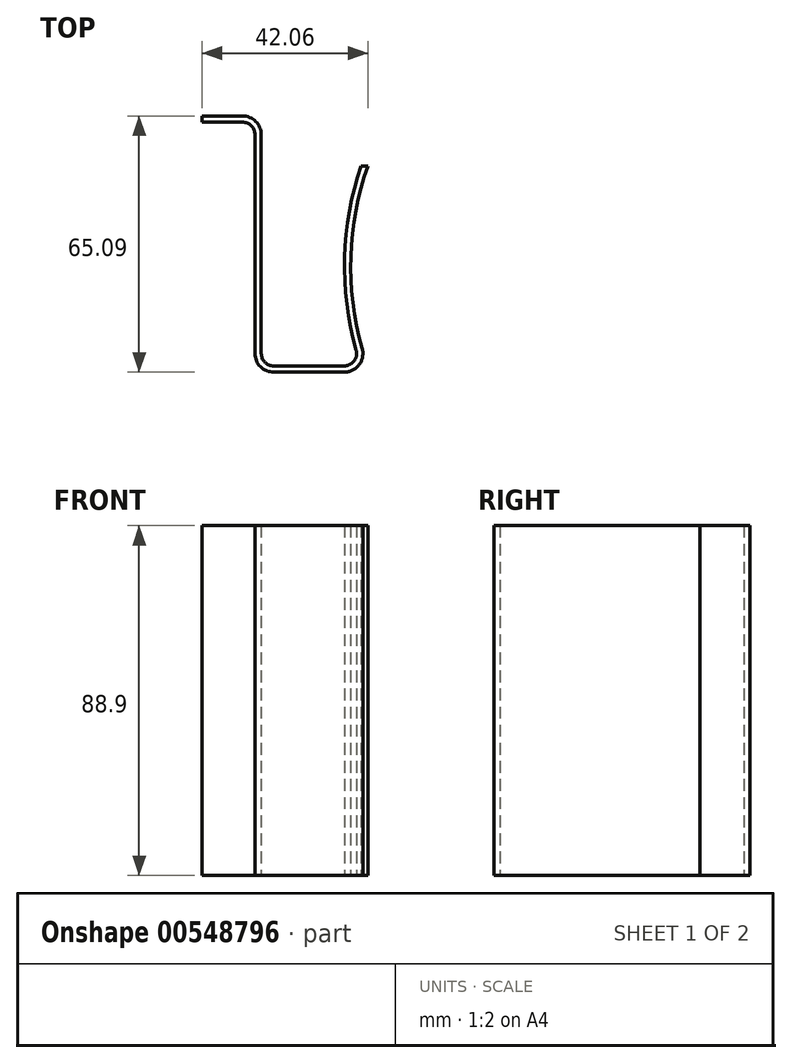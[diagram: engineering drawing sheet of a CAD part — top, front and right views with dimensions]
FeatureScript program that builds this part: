
annotation { "Feature Type Name" : "Feature", "Feature Type Description" : "" }
export const myFeature = defineFeature(function(context is Context, id is Id, definition is map)
    precondition{}
    {
        {
            var Q0;
            Q0=qCreatedBy(makeId("Top.planeOp"),FACE);
            var sketch = newSketch(context, id + "F0", { "sketchPlane" : qUnion([Q0])});
            skLineSegment(sketch, "E0", {"start": v(0, 0) * mm, "end": v(10.22, 0) * mm});
            skLineSegment(sketch, "E1", {"start": v(13.4, -3.18) * mm, "end": v(13.4, -58.74) * mm});
            skLineSegment(sketch, "E2", {"start": v(18.16, -63.5) * mm, "end": v(36.05, -63.5) * mm});
            skLineSegment(sketch, "E3", {"start": v(36.05, -61.91) * mm, "end": v(18.16, -61.91) * mm});
            skLineSegment(sketch, "E4", {"start": v(14.98, -58.74) * mm, "end": v(14.98, -3.18) * mm});
            skLineSegment(sketch, "E5", {"start": v(10.22, 1.59) * mm, "end": v(0, 1.59) * mm});
            skLineSegment(sketch, "E6", {"start": v(0, 1.59) * mm, "end": v(0, 0) * mm});
            skLineSegment(sketch, "E7", {"start": v(13.4, -31.75) * mm, "end": v(14.98, -31.75) * mm, "construction": true});
            skLineSegment(sketch, "E8", {"start": v(27.68, -61.91) * mm, "end": v(27.68, -63.5) * mm, "construction": true});
            skArc(sketch, "E9", {"start": v(40.38, -11.11) * mm, "mid": v(36.15, -34.4) * mm, "end": v(39.1, -57.87) * mm});
            skArc(sketch, "E10", {"start": v(42.06, -11.11) * mm, "mid": v(37.74, -34.16) * mm, "end": v(40.63, -57.43) * mm});
            skLineSegment(sketch, "E11", {"start": v(40.38, -61.91) * mm, "end": v(42.65, -61.91) * mm, "construction": true});
            skLineSegment(sketch, "E12", {"start": v(42.65, -61.91) * mm, "end": v(42.65, -63.5) * mm, "construction": true});
            skLineSegment(sketch, "E13", {"start": v(40.38, -11.11) * mm, "end": v(42.06, -11.11) * mm});
            skLineSegment(sketch, "E14", {"start": v(36.12, -36.51) * mm, "end": v(37.7, -36.51) * mm, "construction": true});
            skPoint(sketch, "E15.visualSharp", {"position": v(40.38, -61.91) * mm});
            skArc(sketch, "E15.filletArc", {"start": v(36.05, -61.91) * mm, "mid": v(38.59, -60.65) * mm, "end": v(39.1, -57.87) * mm});
            skPoint(sketch, "E16.visualSharp", {"position": v(42.65, -63.5) * mm});
            skArc(sketch, "E16.filletArc", {"start": v(36.05, -63.5) * mm, "mid": v(39.86, -61.6) * mm, "end": v(40.63, -57.43) * mm});
            skPoint(sketch, "E17.visualSharp", {"position": v(14.98, -61.91) * mm});
            skArc(sketch, "E17.filletArc", {"start": v(14.98, -58.74) * mm, "mid": v(15.91, -60.98) * mm, "end": v(18.16, -61.91) * mm});
            skPoint(sketch, "E18.visualSharp", {"position": v(13.4, -63.5) * mm});
            skArc(sketch, "E18.filletArc", {"start": v(13.4, -58.74) * mm, "mid": v(14.8, -62.1) * mm, "end": v(18.16, -63.5) * mm});
            skPoint(sketch, "E19.visualSharp", {"position": v(13.4, 0) * mm});
            skArc(sketch, "E19.filletArc", {"start": v(13.4, -3.18) * mm, "mid": v(12.47, -0.93) * mm, "end": v(10.22, 0) * mm});
            skPoint(sketch, "E20.visualSharp", {"position": v(14.98, 1.59) * mm});
            skArc(sketch, "E20.filletArc", {"start": v(14.98, -3.18) * mm, "mid": v(13.59, 0.2) * mm, "end": v(10.22, 1.59) * mm});
            skSolve(sketch);
        }
        {
            var Q0;
            Q0 = qSketchRegion(id + "F0", true);
            extrude(context, id + "F1", {"entities" : qUnion([Q0]), "endBound" : BoundingType.SYMMETRIC, "depth" : 88.9 * mm, "offsetDistance" : 25.4 * mm});
        }
    });
